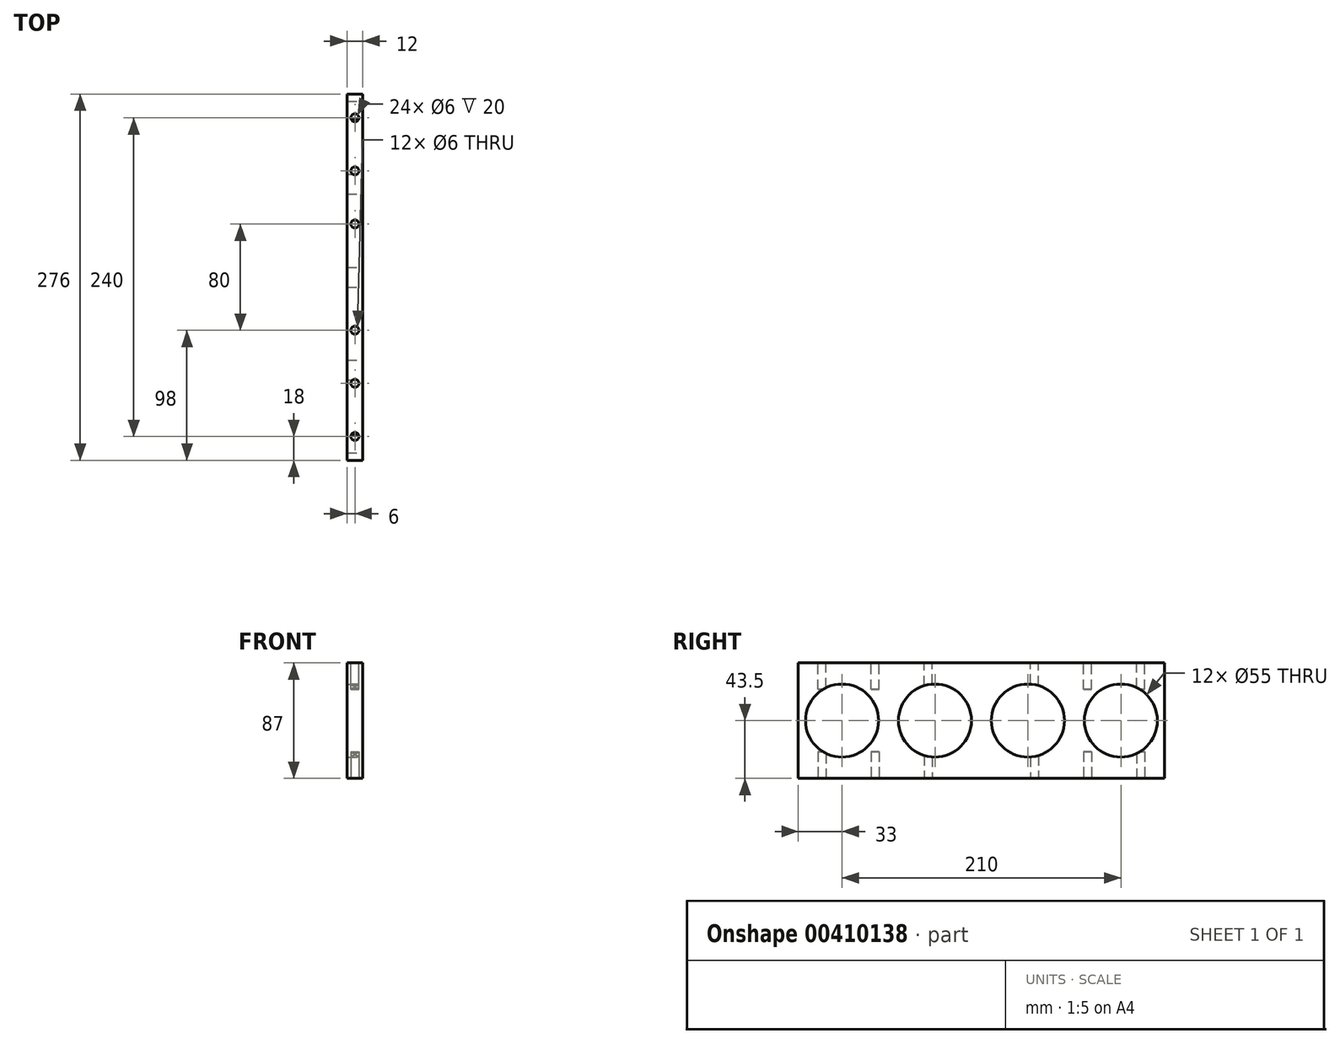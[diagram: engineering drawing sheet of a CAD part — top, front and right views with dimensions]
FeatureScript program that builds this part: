
annotation { "Feature Type Name" : "Feature", "Feature Type Description" : "" }
export const myFeature = defineFeature(function(context is Context, id is Id, definition is map)
    precondition{}
    {
        {
            var Q0;
            Q0=qCreatedBy(makeId("Right.planeOp"),FACE);
            var sketch = newSketch(context, id + "F0", { "sketchPlane" : qUnion([Q0])});
            skLineSegment(sketch, "E0.bottom", {"start": v(0, 0) * mm, "end": v(276, 0) * mm});
            skLineSegment(sketch, "E0.top", {"start": v(0, 87) * mm, "end": v(276, 87) * mm});
            skLineSegment(sketch, "E0.left", {"start": v(0, 0) * mm, "end": v(0, 87) * mm});
            skLineSegment(sketch, "E0.right", {"start": v(276, 0) * mm, "end": v(276, 87) * mm});
            skLineSegment(sketch, "E1", {"start": v(0, 43.5) * mm, "end": v(276, 43.5) * mm, "construction": true});
            skPoint(sketch, "E2", {"position": v(138, 43.5) * mm});
            skSolve(sketch);
        }
        {
            var Q0;
            Q0=qSketchRegion(id+"F0",true);
            extrude(context, id + "F1", {"entities" : qUnion([Q0]), "depth" : 12 * mm});
        }
        {
            var Q0;
            Q0=makeQuery(id+"F1.opExtrude","CAP_FACE",FACE,{"disambiguationData":[OSD([sQuery(id+"F0.wireOp",EDGE,"E0.bottom"),sQuery(id+"F0.wireOp",EDGE,"E0.top"),sQuery(id+"F0.wireOp",EDGE,"E0.left"),sQuery(id+"F0.wireOp",EDGE,"E0.right")])],"isStart":false});
            var sketch = newSketch(context, id + "F2", { "sketchPlane" : qUnion([Q0])});
            skLineSegment(sketch, "E3", {"start": v(138, 87) * mm, "end": v(138, 0) * mm, "construction": true});
            skCircle(sketch, "E4", {"center": v(103, 43.5) * mm, "radius": 27.5 * mm});
            skCircle(sketch, "E5", {"center": v(173, 43.5) * mm, "radius": 27.5 * mm});
            skLineSegment(sketch, "E6", {"start": v(103, 43.5) * mm, "end": v(173, 43.5) * mm, "construction": true});
            skPoint(sketch, "E7", {"position": v(138, 43.5) * mm});
            skLineSegment(sketch, "E8", {"start": v(173, 43.5) * mm, "end": v(243, 43.5) * mm, "construction": true});
            skLineSegment(sketch, "E9", {"start": v(103, 43.5) * mm, "end": v(33, 43.5) * mm, "construction": true});
            skCircle(sketch, "E10", {"center": v(33, 43.5) * mm, "radius": 27.5 * mm});
            skCircle(sketch, "E11", {"center": v(243, 43.5) * mm, "radius": 27.5 * mm});
            skSolve(sketch);
        }
        {
            var Q0;
            Q0 = qSketchRegion(id + "F2", true);
            extrude(context, id + "F3", {"entities" : qUnion([Q0]), "operationType" : NewBodyOperationType.REMOVE, "oppositeDirection" : true, "depth" : 25 * mm});
        }
        {
            var Q0;
            Q0=makeQuery(id+"F1.opExtrude","SWEPT_FACE",FACE,{"disambiguationData":[OSD([sQuery(id+"F0.wireOp",EDGE,"E0.top")])]});
            var sketch = newSketch(context, id + "F4", { "sketchPlane" : qUnion([Q0])});
            skLineSegment(sketch, "E12", {"start": v(6, 276) * mm, "end": v(6, 138) * mm, "construction": true});
            skPoint(sketch, "E12.endSnap0", {"position": v(12, 138) * mm});
            skCircle(sketch, "E13", {"center": v(6, 258) * mm, "radius": 3 * mm});
            skCircle(sketch, "E14.0.1.0", {"center": v(6, 218) * mm, "radius": 3 * mm});
            skCircle(sketch, "E14.0.2.0", {"center": v(6, 178) * mm, "radius": 3 * mm});
            skLineSegment(sketch, "E14.direction1", {"start": v(6, 258) * mm, "end": v(31, 258) * mm, "construction": true});
            skLineSegment(sketch, "E14.direction2", {"start": v(6, 258) * mm, "end": v(6, 218) * mm, "construction": true});
            skLineSegment(sketch, "E15", {"start": v(12, 138) * mm, "end": v(-78.98, 138) * mm, "construction": true});
            skCircle(sketch, "E16.MirrorC", {"center": v(6, 18) * mm, "radius": 3 * mm});
            skCircle(sketch, "E17.MirrorC", {"center": v(6, 58) * mm, "radius": 3 * mm});
            skLineSegment(sketch, "E18.MirrorCS", {"start": v(6, 18) * mm, "end": v(6, 58) * mm, "construction": true});
            skLineSegment(sketch, "E19.MirrorCS", {"start": v(6, 18) * mm, "end": v(31, 18) * mm, "construction": true});
            skCircle(sketch, "E20.MirrorC", {"center": v(6, 98) * mm, "radius": 3 * mm});
            skSolve(sketch);
        }
        {
            var Q0;
            Q0 = qSketchRegion(id + "F4", true);
            extrude(context, id + "F5", {"entities" : qUnion([Q0]), "operationType" : NewBodyOperationType.REMOVE, "oppositeDirection" : true, "depth" : 20 * mm});
        }
        {
            var Q0;
            Q0=makeQuery(id+"F1.opExtrude","SWEPT_FACE",FACE,{"disambiguationData":[OSD([sQuery(id+"F0.wireOp",EDGE,"E0.bottom")])]});
            var sketch = newSketch(context, id + "F6", { "sketchPlane" : qUnion([Q0])});
            skLineSegment(sketch, "E21.0", {"start": v(6, -276) * mm, "end": v(6, -138) * mm});
            skPoint(sketch, "E21.1", {"position": v(12, -138) * mm});
            skCircle(sketch, "E21.2", {"center": v(6, -258) * mm, "radius": 3 * mm});
            skCircle(sketch, "E21.3", {"center": v(6, -218) * mm, "radius": 3 * mm});
            skCircle(sketch, "E21.4", {"center": v(6, -178) * mm, "radius": 3 * mm});
            skLineSegment(sketch, "E21.5", {"start": v(6, -258) * mm, "end": v(31, -258) * mm});
            skLineSegment(sketch, "E21.6", {"start": v(6, -258) * mm, "end": v(6, -218) * mm});
            skLineSegment(sketch, "E21.7", {"start": v(12, -138) * mm, "end": v(-78.98, -138) * mm});
            skCircle(sketch, "E21.8", {"center": v(6, -18) * mm, "radius": 3 * mm});
            skCircle(sketch, "E21.9", {"center": v(6, -58) * mm, "radius": 3 * mm});
            skLineSegment(sketch, "E21.10", {"start": v(6, -18) * mm, "end": v(6, -58) * mm});
            skLineSegment(sketch, "E21.11", {"start": v(6, -18) * mm, "end": v(31, -18) * mm});
            skCircle(sketch, "E21.12", {"center": v(6, -98) * mm, "radius": 3 * mm});
            skSolve(sketch);
        }
        {
            var Q0;
            Q0 = qSketchRegion(id + "F6", true);
            extrude(context, id + "F7", {"entities" : qUnion([Q0]), "operationType" : NewBodyOperationType.REMOVE, "oppositeDirection" : true, "depth" : 20 * mm});
        }
    });
